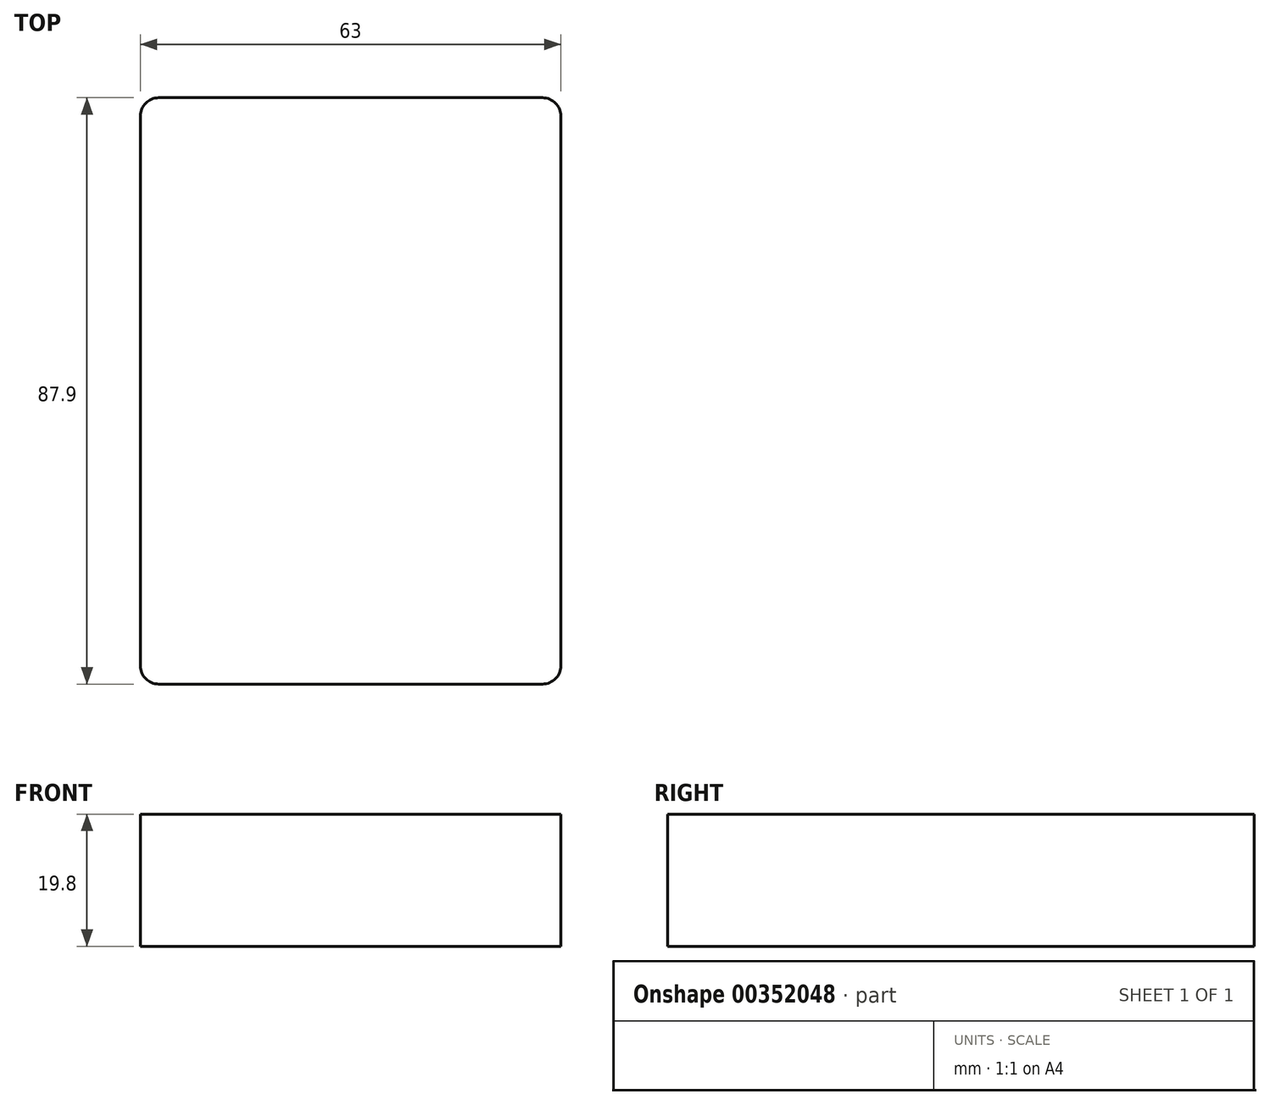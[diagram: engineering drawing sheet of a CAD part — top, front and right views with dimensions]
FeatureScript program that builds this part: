
annotation { "Feature Type Name" : "Feature", "Feature Type Description" : "" }
export const myFeature = defineFeature(function(context is Context, id is Id, definition is map)
    precondition{}
    {
        {
            var Q0;
            Q0=qCreatedBy(makeId("Top.planeOp"),FACE);
            var sketch = newSketch(context, id + "F0", { "sketchPlane" : qUnion([Q0])});
            skLineSegment(sketch, "E0.bottom", {"start": v(-28.75, 43.95) * mm, "end": v(28.75, 43.95) * mm});
            skLineSegment(sketch, "E0.top", {"start": v(-28.75, -43.95) * mm, "end": v(28.75, -43.95) * mm});
            skLineSegment(sketch, "E0.left", {"start": v(-31.5, 41.2) * mm, "end": v(-31.5, -41.2) * mm});
            skLineSegment(sketch, "E0.right", {"start": v(31.5, 41.2) * mm, "end": v(31.5, -41.2) * mm});
            skPoint(sketch, "E0.middle", {"position": v(0, 0) * mm});
            skPoint(sketch, "E1.visualSharp", {"position": v(-31.5, 43.95) * mm});
            skArc(sketch, "E1.filletArc", {"start": v(-28.75, 43.95) * mm, "mid": v(-30.7, 43.14) * mm, "end": v(-31.5, 41.2) * mm});
            skPoint(sketch, "E2.visualSharp", {"position": v(31.5, 43.95) * mm});
            skArc(sketch, "E2.filletArc", {"start": v(31.5, 41.2) * mm, "mid": v(30.7, 43.14) * mm, "end": v(28.75, 43.95) * mm});
            skPoint(sketch, "E3.visualSharp", {"position": v(31.5, -43.95) * mm});
            skArc(sketch, "E3.filletArc", {"start": v(28.75, -43.95) * mm, "mid": v(30.7, -43.14) * mm, "end": v(31.5, -41.2) * mm});
            skPoint(sketch, "E4.visualSharp", {"position": v(-31.5, -43.95) * mm});
            skArc(sketch, "E4.filletArc", {"start": v(-31.5, -41.2) * mm, "mid": v(-30.7, -43.14) * mm, "end": v(-28.75, -43.95) * mm});
            skSolve(sketch);
        }
        {
            var Q0;
            Q0=makeQuery(id+"F0.imprint","IMPRINT",FACE,{"disambiguationData":[TD([[makeQuery(id+"F0.imprint","IMPRINT",EDGE,{"derivedFrom":sQuery(id+"F0.wireOp",EDGE,"E0.bottom")}),-1.0]])]});
            extrude(context, id + "F1", {"entities" : qUnion([Q0]), "depth" : 19.8 * mm});
        }
    });
